# Revit family: SWWZ80x240
name_source: partatom
category: Detail Items
revit_build: Autodesk Revit 2015 (Build: 20140606_1530(x64)
units: mm (PartAtom-declared; Revit-internal decimal feet)

## types (2) — shared parameters
Density = 0.05 kg
Description = Screws
EPD = https://www.strongtie.eu
ETA / DoP = https://www.strongtie.eu
Manufacturer = Simpson Strong-Tie
Model = SWWZ8.0x240
Model Disclaimer = Contact Simpson Strong-Tie Company  for more information
Model ID = 0228433657839304044720475300318295655075
Name = SWWZ8.0x240
ObjectType = SWWZ8.0x240
Product Material = Impreg®+
Product Type = Screws
Reference = 76355
Technical datasheet = https://www.strongtie.eu
URL = www.strongtie.eu
UniClass Number = Pr_20_29_76_98
UniClass Title = Wood screws

## per-type parameters (varying)
| type | _visiblefront | _visibletop |
| SST_SWWZ8.0x240_Front | Yes | No |
| SST_SWWZ8.0x240_Top | No | Yes |

## geometry (parser evidence)
native form markers: Sweep x2
no freeform markers — native parametric forms only
